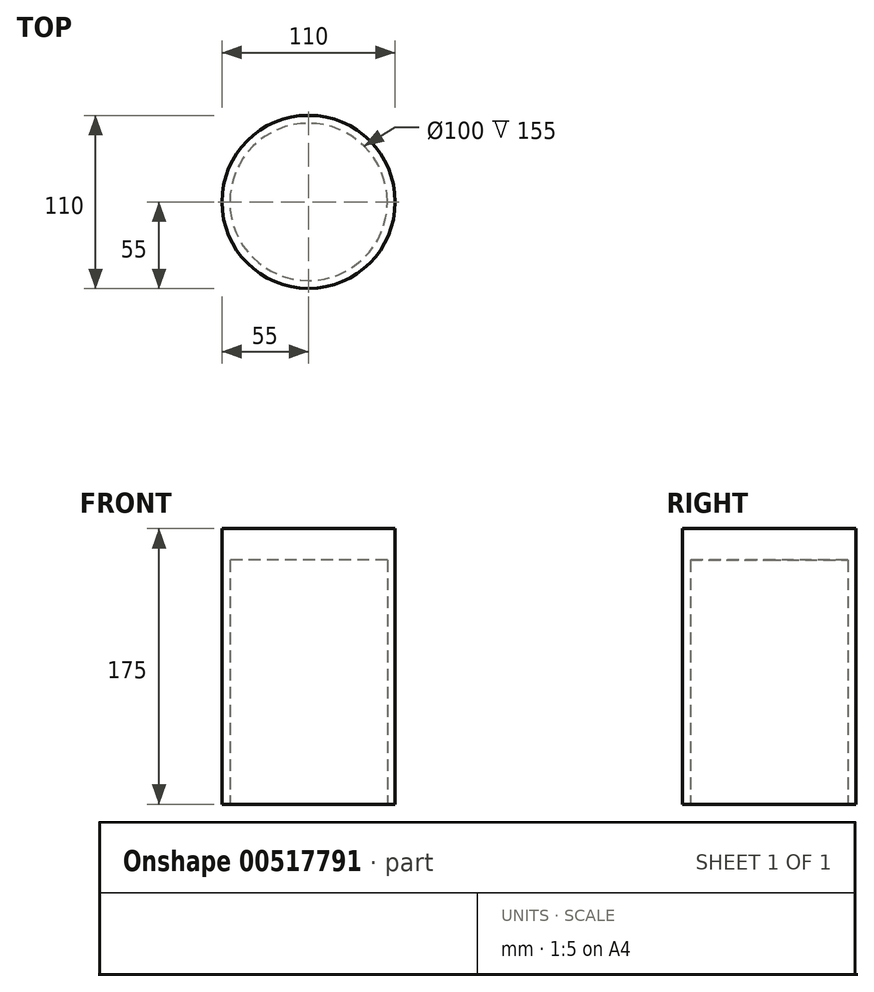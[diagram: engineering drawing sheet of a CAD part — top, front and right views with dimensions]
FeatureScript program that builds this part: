
annotation { "Feature Type Name" : "Feature", "Feature Type Description" : "" }
export const myFeature = defineFeature(function(context is Context, id is Id, definition is map)
    precondition{}
    {
        {
            var Q0;
            Q0=qCreatedBy(makeId("Top.planeOp"),FACE);
            var sketch = newSketch(context, id + "F0", { "sketchPlane" : qUnion([Q0])});
            skCircle(sketch, "E0", {"center": v(0, 0) * mm, "radius": 55 * mm});
            skSolve(sketch);
        }
        {
            var Q0;
            Q0=makeQuery(id+"F0.imprint","IMPRINT",FACE,{"disambiguationData":[TD([[makeQuery(id+"F0.imprint","IMPRINT",EDGE,{"derivedFrom":sQuery(id+"F0.wireOp",EDGE,"E0")}),1.0]])]});
            var sketch = newSketch(context, id + "F1", { "sketchPlane" : qUnion([Q0])});
            skCircle(sketch, "E1", {"center": v(0, 0) * mm, "radius": 50 * mm});
            skSolve(sketch);
        }
        {
            var Q0;
            Q0=makeQuery(id+"F0.imprint","IMPRINT",FACE,{"disambiguationData":[TD([[makeQuery(id+"F0.imprint","IMPRINT",EDGE,{"derivedFrom":sQuery(id+"F0.wireOp",EDGE,"E0")}),1.0]])]});
            extrude(context, id + "F2", {"entities" : qUnion([Q0]), "depth" : 175 * mm, "offsetDistance" : 25 * mm});
        }
        {
            var Q0;
            Q0=makeQuery(id+"F1.imprint","IMPRINT",FACE,{"disambiguationData":[TD([[makeQuery(id+"F1.imprint","IMPRINT",EDGE,{"derivedFrom":sQuery(id+"F1.wireOp",EDGE,"E1")}),1.0]])]});
            extrude(context, id + "F3", {"entities" : qUnion([Q0]), "operationType" : NewBodyOperationType.REMOVE, "depth" : 155 * mm, "offsetDistance" : 25 * mm});
        }
    });
